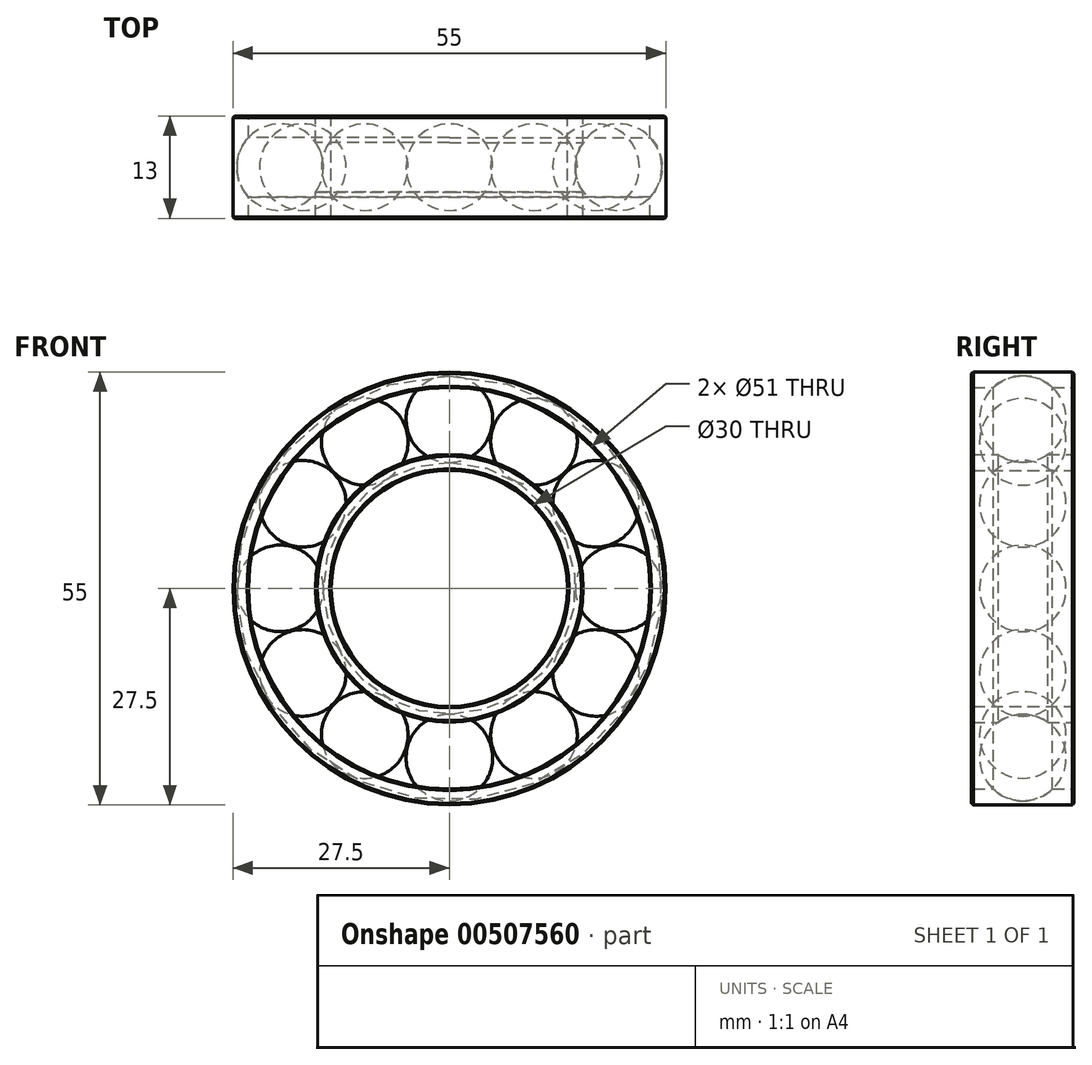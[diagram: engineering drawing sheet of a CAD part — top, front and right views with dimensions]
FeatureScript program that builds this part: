
annotation { "Feature Type Name" : "Feature", "Feature Type Description" : "" }
export const myFeature = defineFeature(function(context is Context, id is Id, definition is map)
    precondition{}
    {
        {
            var Q0;
            Q0=qCreatedBy(makeId("Front.planeOp"),FACE);
            var sketch = newSketch(context, id + "F0", { "sketchPlane" : qUnion([Q0])});
            skCircle(sketch, "E0", {"center": v(0, 0) * mm, "radius": 15 * mm});
            skCircle(sketch, "E1", {"center": v(0, 0) * mm, "radius": 17 * mm});
            skCircle(sketch, "E2", {"center": v(0, 0) * mm, "radius": 25.5 * mm});
            skCircle(sketch, "E3", {"center": v(0, 0) * mm, "radius": 27.5 * mm});
            skSolve(sketch);
        }
        {
            var Q0;
            Q0=makeQuery(id+"F0.imprint","IMPRINT",FACE,{"disambiguationData":[TD([[makeQuery(id+"F0.imprint","IMPRINT",EDGE,{"derivedFrom":sQuery(id+"F0.wireOp",EDGE,"E2")}),-1.0]])]});
            var Q1;
            Q1=makeQuery(id+"F0.imprint","IMPRINT",FACE,{"disambiguationData":[TD([[makeQuery(id+"F0.imprint","IMPRINT",EDGE,{"derivedFrom":sQuery(id+"F0.wireOp",EDGE,"E0")}),-1.0]])]});
            extrude(context, id + "F1", {"entities" : qUnion([Q0, Q1]), "depth" : 13 * mm, "symmetric" : true});
        }
        {
            var Q0;
            Q0=qCreatedBy(makeId("Top.planeOp"),FACE);
            var sketch = newSketch(context, id + "F2", { "sketchPlane" : qUnion([Q0])});
            skCircle(sketch, "E4", {"center": v(-21.5, 0) * mm, "radius": 5.5 * mm});
            skSolve(sketch);
        }
        {
            var Q0;
            Q0=makeQuery(id+"F2.imprint","IMPRINT",FACE,{"disambiguationData":[TD([[makeQuery(id+"F2.imprint","IMPRINT",EDGE,{"derivedFrom":sQuery(id+"F2.wireOp",EDGE,"E4")}),1.0]])]});
            var Q1;
            Q1=sQuery(id+"F2.wireOp",EDGE,"E4");
            var Q2;
            Q2=makeQuery(id+"F1.opExtrude","CAP_EDGE",EDGE,{"disambiguationData":[OSD([sQuery(id+"F0.wireOp",EDGE,"E1")])],"isStart":false});
            revolve(context, id + "F3", {"operationType" : NewBodyOperationType.REMOVE, "entities" : qUnion([Q0]), "surfaceEntities" : qUnion([Q1]), "axis" : qUnion([Q2]), "revolveType" : RevolveType.FULL});
        }
        {
            var Q0;
            Q0=qCreatedBy(makeId("Top.planeOp"),FACE);
            var sketch = newSketch(context, id + "F4", { "sketchPlane" : qUnion([Q0])});
            skArc(sketch, "E5", {"start": v(-16, 0) * mm, "mid": v(-21.5, 5.5) * mm, "end": v(-27, 0) * mm});
            skLineSegment(sketch, "E6", {"start": v(-16, 0) * mm, "end": v(-27, 0) * mm});
            skSolve(sketch);
        }
        {
            var Q0;
            Q0=makeQuery(id+"F4.imprint","IMPRINT",FACE,{"disambiguationData":[TD([[makeQuery(id+"F4.imprint","IMPRINT",EDGE,{"derivedFrom":sQuery(id+"F4.wireOp",EDGE,"E5")}),1.0]])]});
            var Q1;
            Q1=sQuery(id+"F4.wireOp",EDGE,"E6");
            revolve(context, id + "F5", {"entities" : qUnion([Q0]), "axis" : qUnion([Q1]), "revolveType" : RevolveType.FULL});
        }
        {
            var Q0;
            Q0=makeQuery(id+"F5.opRevolve","SWEPT_BODY",BODY,{"disambiguationData":[OSD([sQuery(id+"F4.wireOp",EDGE,"E5"),sQuery(id+"F4.wireOp",EDGE,"E6")])]});
            var Q1;
            Q1=makeQuery(id+"F1.opExtrude","CAP_EDGE",EDGE,{"disambiguationData":[OSD([sQuery(id+"F0.wireOp",EDGE,"E2")])],"isStart":false});
            circularPattern(context, id + "F6", {"entities" : qUnion([Q0]), "axis" : qUnion([Q1]), "angle" : 360 * degree, "instanceCount" : 12, "equalSpace" : true});
        }
        {
            var Q0;
            Q0=makeQuery(id+"F1.opExtrude","CAP_EDGE",EDGE,{"disambiguationData":[OSD([sQuery(id+"F0.wireOp",EDGE,"E0")])],"isStart":false});
            var Q1;
            Q1=makeQuery(id+"F1.opExtrude","CAP_EDGE",EDGE,{"disambiguationData":[OSD([sQuery(id+"F0.wireOp",EDGE,"E1")])],"isStart":false});
            var Q2;
            Q2=makeQuery(id+"F1.opExtrude","CAP_EDGE",EDGE,{"disambiguationData":[OSD([sQuery(id+"F0.wireOp",EDGE,"E2")])],"isStart":false});
            var Q3;
            Q3=makeQuery(id+"F1.opExtrude","CAP_EDGE",EDGE,{"disambiguationData":[OSD([sQuery(id+"F0.wireOp",EDGE,"E3")])],"isStart":false});
            var Q4;
            Q4=makeQuery(id+"F1.opExtrude","CAP_EDGE",EDGE,{"disambiguationData":[OSD([sQuery(id+"F0.wireOp",EDGE,"E0")])],"isStart":true});
            var Q5;
            Q5=makeQuery(id+"F1.opExtrude","CAP_EDGE",EDGE,{"disambiguationData":[OSD([sQuery(id+"F0.wireOp",EDGE,"E1")])],"isStart":true});
            var Q6;
            Q6=makeQuery(id+"F1.opExtrude","CAP_EDGE",EDGE,{"disambiguationData":[OSD([sQuery(id+"F0.wireOp",EDGE,"E2")])],"isStart":true});
            var Q7;
            Q7=makeQuery(id+"F1.opExtrude","CAP_EDGE",EDGE,{"disambiguationData":[OSD([sQuery(id+"F0.wireOp",EDGE,"E3")])],"isStart":true});
            chamfer(context, id + "F7", {"entities" : qUnion([Q0, Q1, Q2, Q3, Q4, Q5, Q6, Q7]), "width" : 0.2 * mm, "tangentPropagation" : true});
        }
    });
